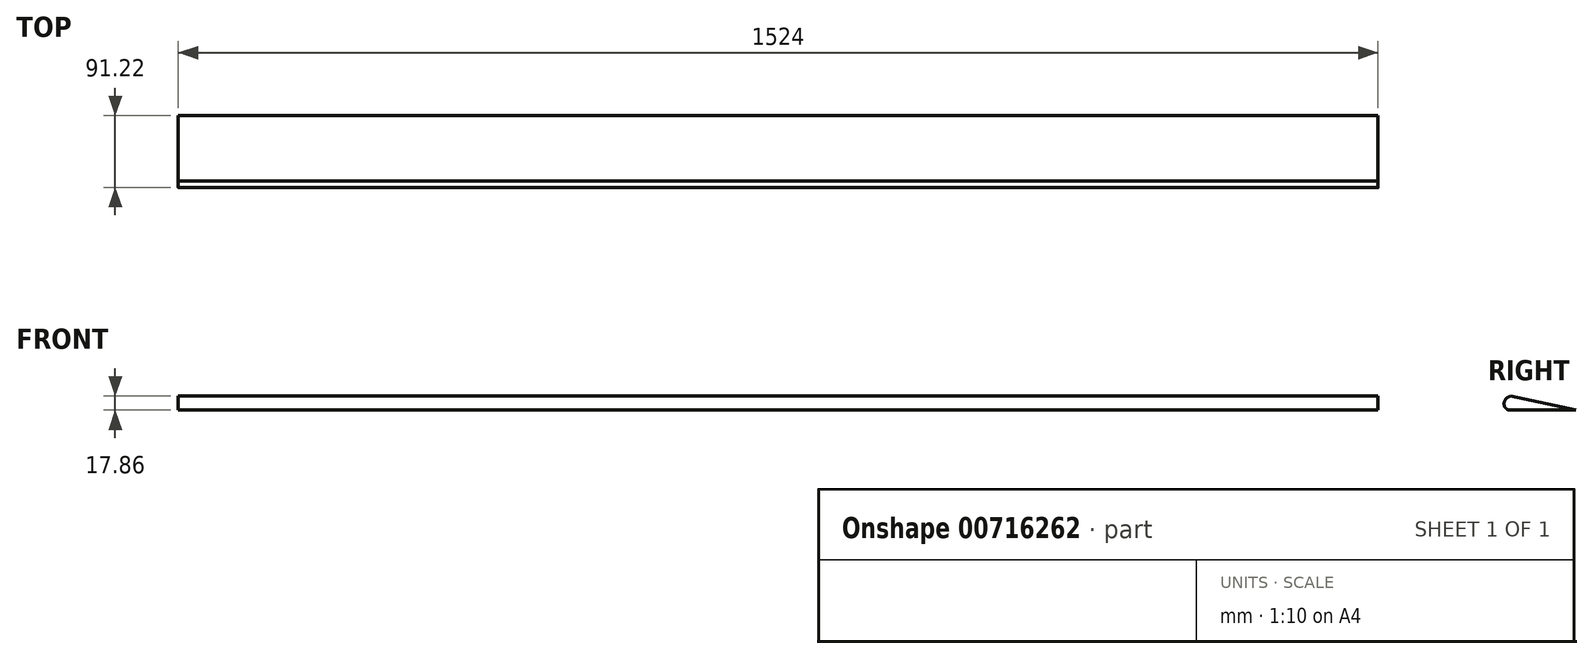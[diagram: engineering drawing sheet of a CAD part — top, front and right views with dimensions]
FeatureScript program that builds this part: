
annotation { "Feature Type Name" : "Feature", "Feature Type Description" : "" }
export const myFeature = defineFeature(function(context is Context, id is Id, definition is map)
    precondition{}
    {
        {
            var Q0;
            Q0=qCreatedBy(makeId("Right.planeOp"),FACE);
            var sketch = newSketch(context, id + "F0", { "sketchPlane" : qUnion([Q0])});
            skLineSegment(sketch, "E0", {"start": v(-39.62, 0) * mm, "end": v(43.57, 0) * mm});
            skArc(sketch, "E1", {"start": v(-39.62, 0) * mm, "mid": v(-45.81, 2.92) * mm, "end": v(-47.5, 9.54) * mm});
            skArc(sketch, "E2", {"start": v(-47.5, 9.54) * mm, "mid": v(-44.78, 14.85) * mm, "end": v(-39.62, 17.86) * mm});
            skLineSegment(sketch, "E3", {"start": v(-39.62, 17.86) * mm, "end": v(43.57, 0) * mm});
            skSolve(sketch);
        }
        {
            var Q0;
            Q0 = qSketchRegion(id + "F0", true);
            extrude(context, id + "F1", {"entities" : qUnion([Q0]), "depth" : 1524 * mm, "offsetDistance" : 25.4 * mm});
        }
    });
